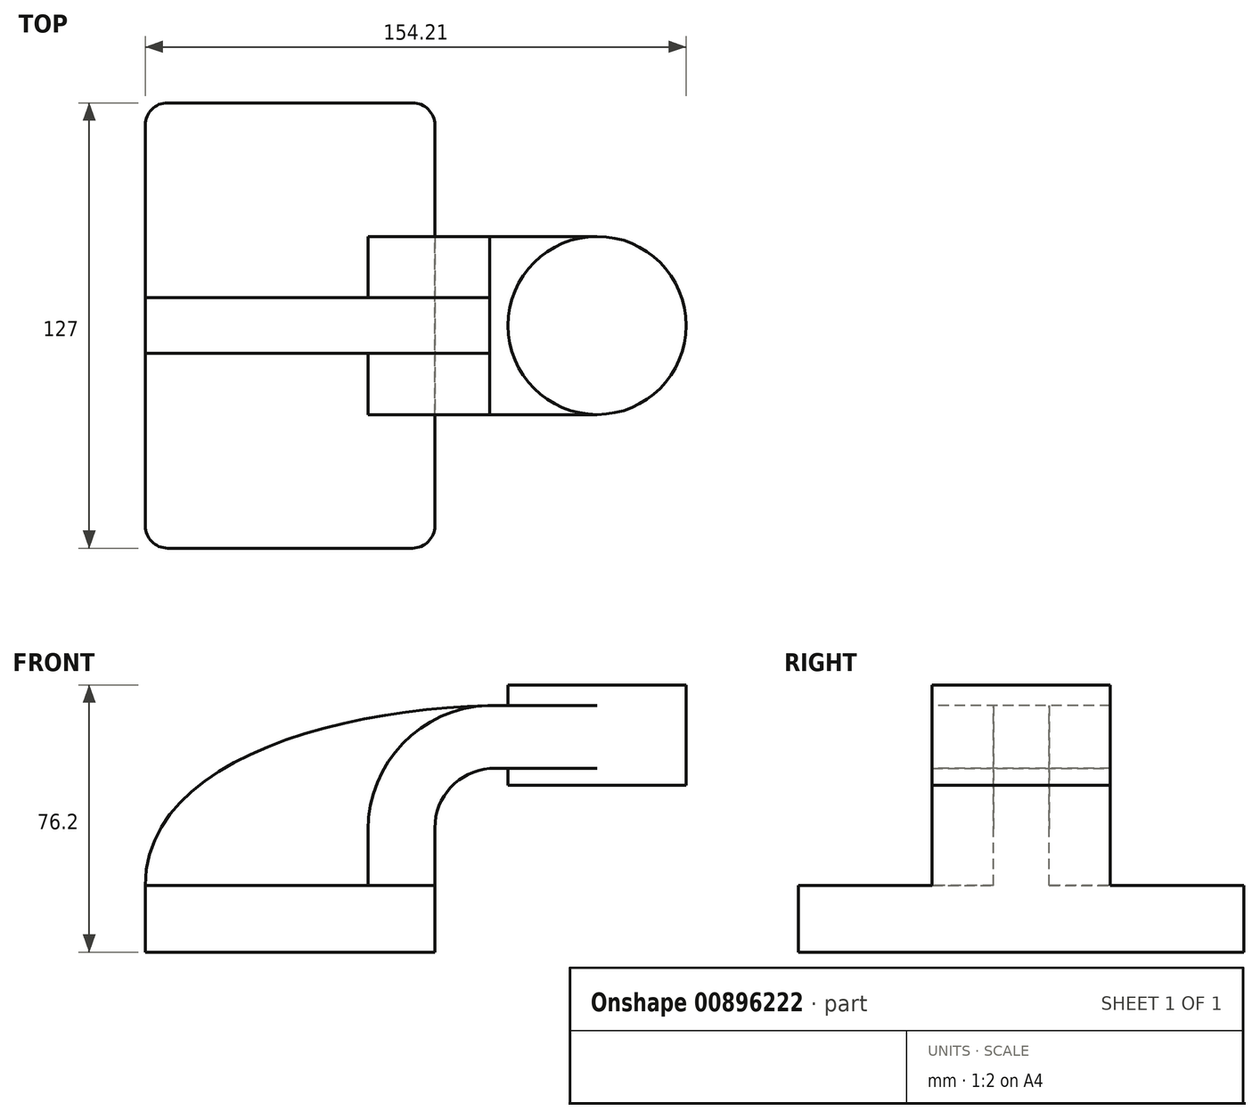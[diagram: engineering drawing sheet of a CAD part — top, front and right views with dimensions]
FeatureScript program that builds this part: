
annotation { "Feature Type Name" : "Feature", "Feature Type Description" : "" }
export const myFeature = defineFeature(function(context is Context, id is Id, definition is map)
    precondition{}
    {
        {
            var Q0;
            Q0=qCreatedBy(makeId("Front.planeOp"),FACE);
            var sketch = newSketch(context, id + "F0", { "sketchPlane" : qUnion([Q0])});
            skLineSegment(sketch, "E0.bottom", {"start": v(-24.62, 20.18) * mm, "end": v(57.93, 20.18) * mm});
            skLineSegment(sketch, "E0.top", {"start": v(-24.62, 1.13) * mm, "end": v(57.93, 1.13) * mm});
            skLineSegment(sketch, "E0.left", {"start": v(-24.62, 20.18) * mm, "end": v(-24.62, 1.13) * mm});
            skLineSegment(sketch, "E0.right", {"start": v(57.93, 20.18) * mm, "end": v(57.93, 1.13) * mm});
            skLineSegment(sketch, "E1.bottom", {"start": v(78.79, 77.33) * mm, "end": v(129.59, 77.33) * mm});
            skLineSegment(sketch, "E1.top", {"start": v(78.79, 48.76) * mm, "end": v(129.59, 48.76) * mm});
            skLineSegment(sketch, "E1.left", {"start": v(78.79, 77.33) * mm, "end": v(78.79, 48.76) * mm});
            skLineSegment(sketch, "E1.right", {"start": v(129.59, 77.33) * mm, "end": v(129.59, 48.76) * mm});
            skPoint(sketch, "E2", {"position": v(104.19, 63.04) * mm});
            skPoint(sketch, "E3.orphan", {"position": v(78.79, 63.04) * mm});
            skPoint(sketch, "E4.orphan", {"position": v(104.19, 77.33) * mm});
            skPoint(sketch, "E5.end.orphan", {"position": v(129.59, 63.04) * mm});
            skPoint(sketch, "E6.end.orphan", {"position": v(104.19, 48.76) * mm});
            skLineSegment(sketch, "E7", {"start": v(38.88, 20.18) * mm, "end": v(38.88, 36.02) * mm});
            skLineSegment(sketch, "E8", {"start": v(104.19, 77.33) * mm, "end": v(104.19, 48.76) * mm});
            skLineSegment(sketch, "E9", {"start": v(57.93, 20.18) * mm, "end": v(57.93, 36.53) * mm});
            skArc(sketch, "E10", {"start": v(73.58, 53.53) * mm, "mid": v(62.44, 48.08) * mm, "end": v(57.93, 36.53) * mm});
            skLineSegment(sketch, "E11", {"start": v(73.58, 53.53) * mm, "end": v(104.19, 53.53) * mm});
            skArc(sketch, "E12", {"start": v(73.58, 71.5) * mm, "mid": v(49, 60.83) * mm, "end": v(38.88, 36.02) * mm});
            skLineSegment(sketch, "E13", {"start": v(73.58, 71.5) * mm, "end": v(104.19, 71.5) * mm});
            skFitSpline(sketch, "E14", {"points": [v(-24.62, 20.18) * mm, v(73.58, 71.5) * mm], "startDerivative": vector(0.5, 106.72) * mm, "endDerivative": vector(132.25, 3.75) * mm});
            skSolve(sketch);
        }
        {
            var Q0;
            Q0=makeQuery(id+"F0.imprint","IMPRINT",FACE,{"disambiguationData":[TD([[makeQuery(id+"F0.imprint","IMPRINT",EDGE,{"derivedFrom":sQuery(id+"F0.wireOp",EDGE,"E0.top")}),1.0]])]});
            extrude(context, id + "F1", {"entities" : qUnion([Q0]), "endBound" : BoundingType.SYMMETRIC, "oppositeDirection" : true, "depth" : 127 * mm, "offsetDistance" : 25.4 * mm});
        }
        {
            var Q0;
            {var subQ0=sQuery(id+"F0.wireOp",EDGE,"E13");var subQ1=sQuery(id+"F0.wireOp",EDGE,"E1.left");var subQ2=makeQuery(id+"F0.imprint","INTERSECT",VERTEX,{"derivedFrom":[subQ1,subQ0]});Q0=makeQuery(id+"F0.imprint","IMPRINT",FACE,{"disambiguationData":[TD([[makeQuery(id+"F0.imprint","IMPRINT",EDGE,{"disambiguationData":[TD([[subQ2,-1.0]])],"derivedFrom":subQ1}),1.0]])]});}
            var Q1;
            {var subQ1=sQuery(id+"F0.wireOp",EDGE,"E7");Q1=makeQuery(id+"F0.imprint","IMPRINT",FACE,{"disambiguationData":[TD([[makeQuery(id+"F0.imprint","IMPRINT",EDGE,{"derivedFrom":subQ1}),-1.0]])]});}
            extrude(context, id + "F2", {"entities" : qUnion([Q0, Q1]), "operationType" : NewBodyOperationType.ADD, "endBound" : BoundingType.SYMMETRIC, "depth" : 50.8 * mm, "offsetDistance" : 25.4 * mm});
        }
        {
            var Q0;
            {var subQ3=sQuery(id+"F0.wireOp",EDGE,"E7");Q0=makeQuery(id+"F0.imprint","IMPRINT",FACE,{"disambiguationData":[TD([[makeQuery(id+"F0.imprint","IMPRINT",EDGE,{"derivedFrom":subQ3}),1.0]])]});}
            extrude(context, id + "F3", {"entities" : qUnion([Q0]), "operationType" : NewBodyOperationType.ADD, "endBound" : BoundingType.SYMMETRIC, "depth" : 15.88 * mm, "offsetDistance" : 25.4 * mm});
        }
        {
            var Q0;
            {var subQ4=sQuery(id+"F0.wireOp",EDGE,"E1.right");Q0=makeQuery(id+"F0.imprint","IMPRINT",FACE,{"disambiguationData":[TD([[makeQuery(id+"F0.imprint","IMPRINT",EDGE,{"derivedFrom":subQ4}),-1.0]])]});}
            var Q1;
            Q1=sQuery(id+"F0.wireOp",EDGE,"E8");
            var Q2;
            Q2=sQuery(id+"F0.wireOp",EDGE,"E1.left");
            var Q3;
            Q3=sQuery(id+"F0.wireOp",EDGE,"E1.bottom");
            var Q4;
            Q4=sQuery(id+"F0.wireOp",EDGE,"E1.right");
            var Q5;
            Q5=sQuery(id+"F0.wireOp",EDGE,"E1.top");
            var Q6;
            Q6=sQuery(id+"F0.wireOp",EDGE,"E8");
            revolve(context, id + "F4", {"operationType" : NewBodyOperationType.ADD, "surfaceOperationType" : NewSurfaceOperationType.NEW, "entities" : qUnion([Q0]), "surfaceEntities" : qUnion([Q1, Q2, Q3, Q4, Q5]), "axis" : qUnion([Q6]), "revolveType" : RevolveType.FULL});
        }
        {
            var Q0;
            Q0=makeQuery(id+"F1.opExtrude","CAP_EDGE",EDGE,{"disambiguationData":[OSD([sQuery(id+"F0.wireOp",EDGE,"E0.right")])],"isStart":false});
            var Q1;
            Q1=makeQuery(id+"F1.opExtrude","CAP_EDGE",EDGE,{"disambiguationData":[OSD([sQuery(id+"F0.wireOp",EDGE,"E0.right")])],"isStart":true});
            var Q2;
            Q2=makeQuery(id+"F1.opExtrude","CAP_EDGE",EDGE,{"disambiguationData":[OSD([sQuery(id+"F0.wireOp",EDGE,"E0.left")])],"isStart":false});
            var Q3;
            Q3=makeQuery(id+"F1.opExtrude","CAP_EDGE",EDGE,{"disambiguationData":[OSD([sQuery(id+"F0.wireOp",EDGE,"E0.left")])],"isStart":true});
            fillet(context, id + "F5", {"entities" : qUnion([Q0, Q1, Q2, Q3]), "radius" : 6.35 * mm, "tangentPropagation" : true, "allowEdgeOverflow" : false});
        }
    });
